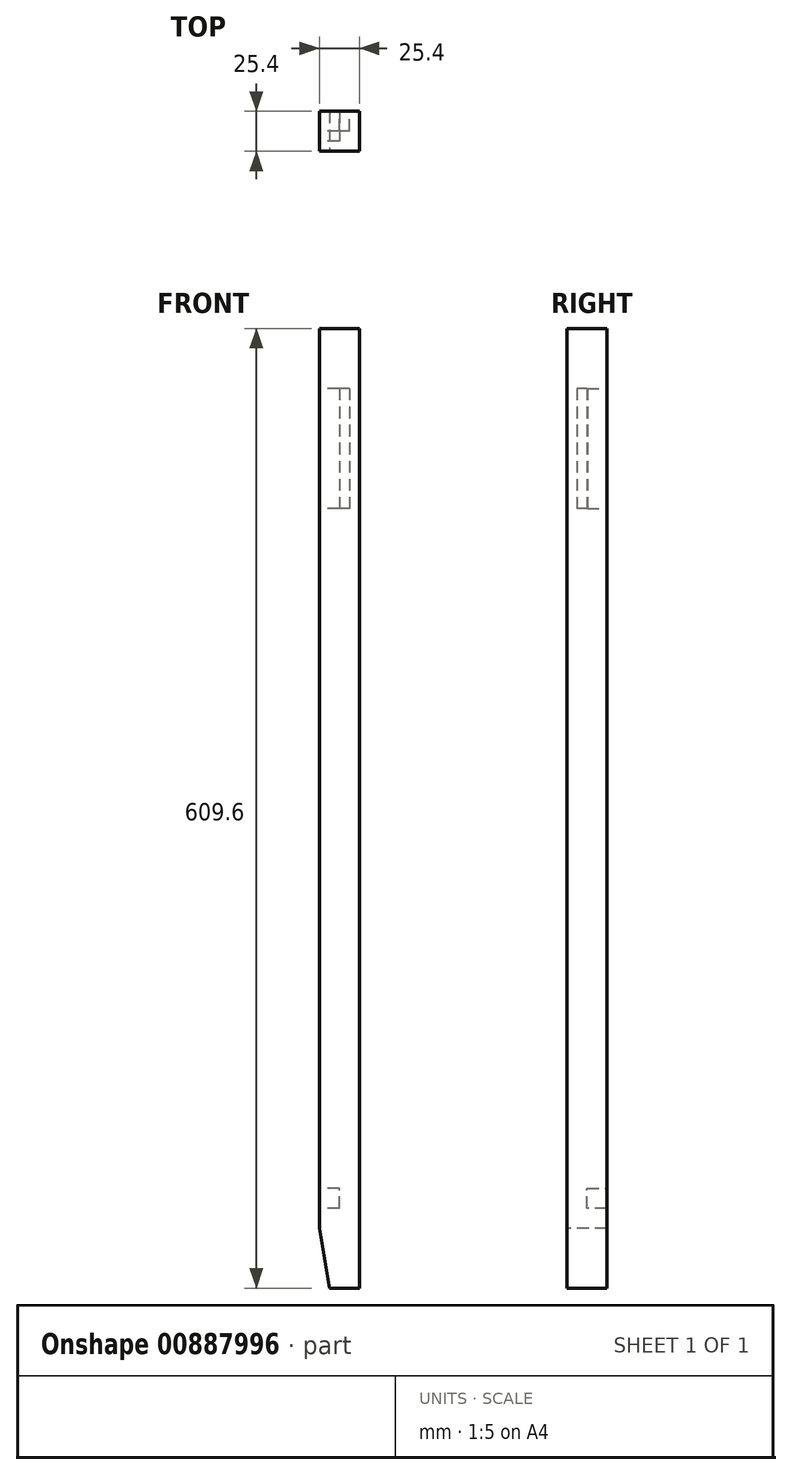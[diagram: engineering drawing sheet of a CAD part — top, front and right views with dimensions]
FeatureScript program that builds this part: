
annotation { "Feature Type Name" : "Feature", "Feature Type Description" : "" }
export const myFeature = defineFeature(function(context is Context, id is Id, definition is map)
    precondition{}
    {
        {
            var Q0;
            Q0=qCreatedBy(makeId("Front.planeOp"),FACE);
            var sketch = newSketch(context, id + "F0", { "sketchPlane" : qUnion([Q0])});
            skLineSegment(sketch, "E0.bottom", {"start": v(12.7, -304.8) * mm, "end": v(-12.7, -304.8) * mm});
            skLineSegment(sketch, "E0.top", {"start": v(12.7, 304.8) * mm, "end": v(-12.7, 304.8) * mm});
            skLineSegment(sketch, "E0.left", {"start": v(12.7, -304.8) * mm, "end": v(12.7, 304.8) * mm});
            skLineSegment(sketch, "E0.right", {"start": v(-12.7, -304.8) * mm, "end": v(-12.7, 304.8) * mm});
            skPoint(sketch, "E0.middle", {"position": v(0, 0) * mm});
            skSolve(sketch);
        }
        {
            var Q0;
            Q0 = qSketchRegion(id + "F0", true);
            extrude(context, id + "F1", {"entities" : qUnion([Q0]), "depth" : 25.4 * mm, "offsetDistance" : 25.4 * mm});
        }
        {
            var Q0;
            Q0=makeQuery(id+"F1.opExtrude","CAP_FACE",FACE,{"disambiguationData":[OSD([sQuery(id+"F0.wireOp",EDGE,"E0.bottom"),sQuery(id+"F0.wireOp",EDGE,"E0.top"),sQuery(id+"F0.wireOp",EDGE,"E0.left"),sQuery(id+"F0.wireOp",EDGE,"E0.right")])],"isStart":false});
            var sketch = newSketch(context, id + "F2", { "sketchPlane" : qUnion([Q0])});
            skLineSegment(sketch, "E1", {"start": v(-6.35, -304.8) * mm, "end": v(-12.7, -266.7) * mm});
            skLineSegment(sketch, "E2", {"start": v(-12.7, -266.7) * mm, "end": v(-12.7, -304.8) * mm});
            skLineSegment(sketch, "E3", {"start": v(-12.7, -304.8) * mm, "end": v(-6.35, -304.8) * mm});
            skSolve(sketch);
        }
        {
            var Q0;
            Q0 = qSketchRegion(id + "F2", true);
            extrude(context, id + "F3", {"entities" : qUnion([Q0]), "operationType" : NewBodyOperationType.REMOVE, "oppositeDirection" : true, "depth" : 25.4 * mm, "offsetDistance" : 25.4 * mm});
        }
        {
            var Q0;
            Q0=makeQuery(id+"F1.opExtrude","SWEPT_FACE",FACE,{"disambiguationData":[OSD([sQuery(id+"F0.wireOp",EDGE,"E0.right")])]});
            var sketch = newSketch(context, id + "F4", { "sketchPlane" : qUnion([Q0])});
            skLineSegment(sketch, "E4", {"start": v(0, -254) * mm, "end": v(12.7, -254) * mm});
            skLineSegment(sketch, "E5", {"start": v(12.7, -254) * mm, "end": v(12.7, -241.3) * mm});
            skLineSegment(sketch, "E6", {"start": v(12.7, -241.3) * mm, "end": v(0, -241.3) * mm});
            skLineSegment(sketch, "E7", {"start": v(0, -241.3) * mm, "end": v(0, -254) * mm});
            skSolve(sketch);
        }
        {
            var Q0;
            Q0 = qSketchRegion(id + "F4", true);
            extrude(context, id + "F5", {"entities" : qUnion([Q0]), "operationType" : NewBodyOperationType.REMOVE, "oppositeDirection" : true, "depth" : 12.7 * mm, "offsetDistance" : 25.4 * mm});
        }
        {
            var Q0;
            Q0=makeQuery(id+"F1.opExtrude","SWEPT_FACE",FACE,{"disambiguationData":[OSD([sQuery(id+"F0.wireOp",EDGE,"E0.right")])]});
            var sketch = newSketch(context, id + "F6", { "sketchPlane" : qUnion([Q0])});
            skLineSegment(sketch, "E8.bottom", {"start": v(12.7, 266.7) * mm, "end": v(19.05, 266.7) * mm});
            skLineSegment(sketch, "E8.top", {"start": v(12.7, 190.5) * mm, "end": v(19.05, 190.5) * mm});
            skLineSegment(sketch, "E8.left", {"start": v(12.7, 266.7) * mm, "end": v(12.7, 190.5) * mm});
            skLineSegment(sketch, "E8.right", {"start": v(19.05, 266.7) * mm, "end": v(19.05, 190.5) * mm});
            skSolve(sketch);
        }
        {
            var Q0;
            Q0 = qSketchRegion(id + "F6", true);
            extrude(context, id + "F7", {"entities" : qUnion([Q0]), "operationType" : NewBodyOperationType.REMOVE, "oppositeDirection" : true, "depth" : 12.7 * mm, "offsetDistance" : 25.4 * mm});
        }
        {
            var Q0;
            Q0=makeQuery(id+"F1.opExtrude","CAP_FACE",FACE,{"disambiguationData":[OSD([sQuery(id+"F0.wireOp",EDGE,"E0.bottom"),sQuery(id+"F0.wireOp",EDGE,"E0.top"),sQuery(id+"F0.wireOp",EDGE,"E0.left"),sQuery(id+"F0.wireOp",EDGE,"E0.right")])],"isStart":true});
            var sketch = newSketch(context, id + "F8", { "sketchPlane" : qUnion([Q0])});
            skLineSegment(sketch, "E9.bottom", {"start": v(-6.35, 266.7) * mm, "end": v(0, 266.7) * mm});
            skLineSegment(sketch, "E9.top", {"start": v(-6.35, 190.5) * mm, "end": v(0, 190.5) * mm});
            skLineSegment(sketch, "E9.left", {"start": v(-6.35, 266.7) * mm, "end": v(-6.35, 190.5) * mm});
            skLineSegment(sketch, "E9.right", {"start": v(0, 266.7) * mm, "end": v(0, 190.5) * mm});
            skSolve(sketch);
        }
        {
            var Q0;
            Q0 = qSketchRegion(id + "F8", true);
            extrude(context, id + "F9", {"entities" : qUnion([Q0]), "operationType" : NewBodyOperationType.REMOVE, "oppositeDirection" : true, "depth" : 12.45 * mm, "offsetDistance" : 25.4 * mm});
        }
    });
